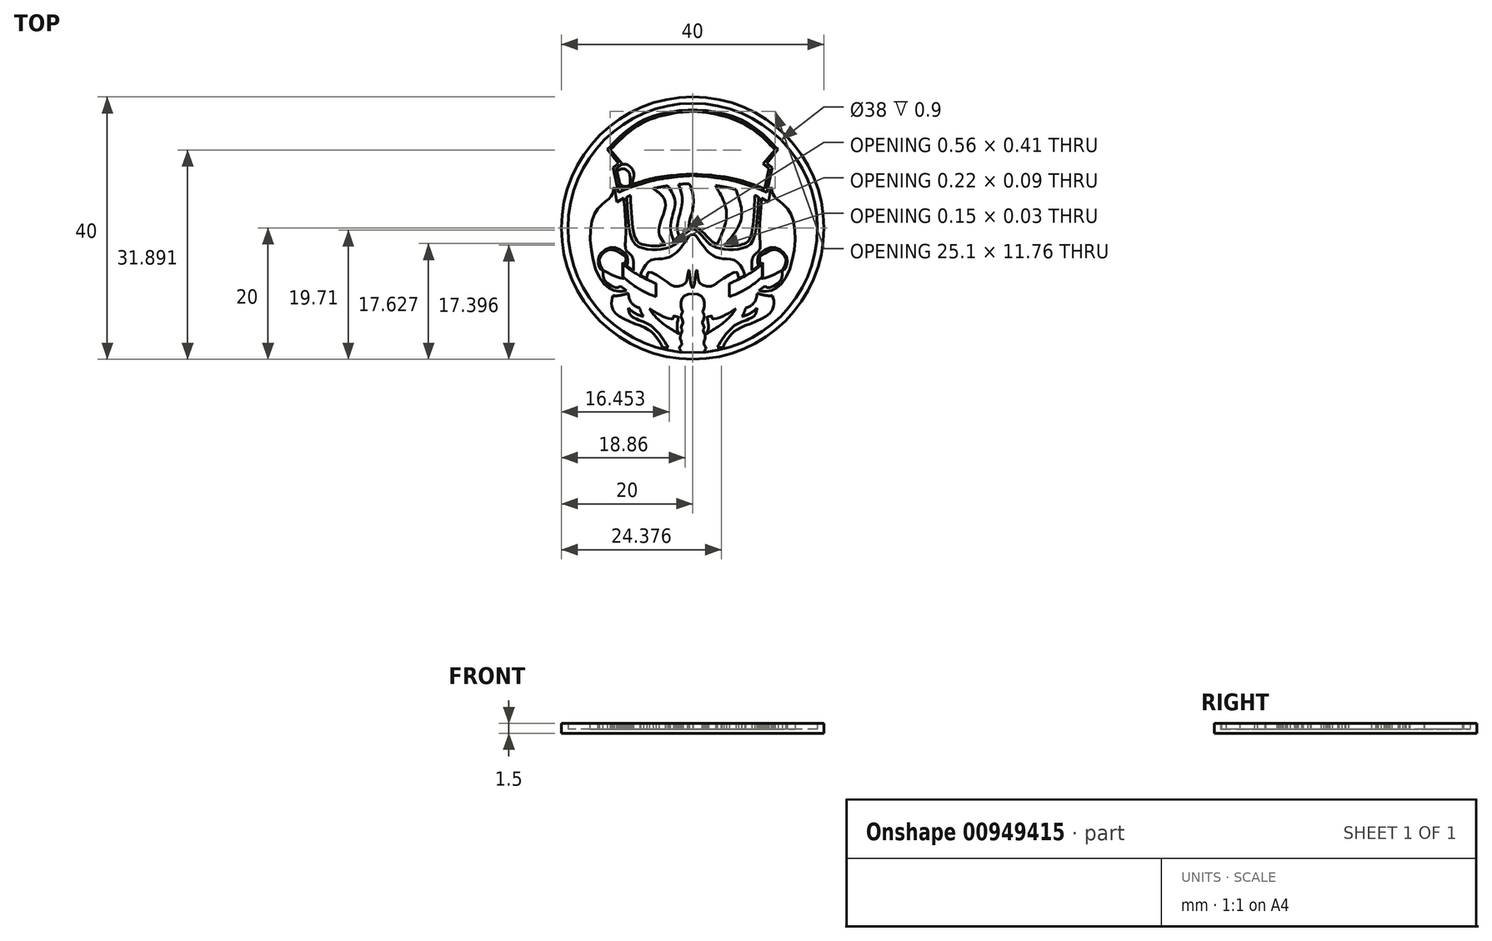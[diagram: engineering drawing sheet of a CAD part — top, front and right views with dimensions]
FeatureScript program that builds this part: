
annotation { "Feature Type Name" : "Feature", "Feature Type Description" : "" }
export const myFeature = defineFeature(function(context is Context, id is Id, definition is map)
    precondition{}
    {
        {
            var Q0;
            Q0=qCreatedBy(makeId("Top.planeOp"),FACE);
            var sketch = newSketch(context, id + "F0", { "sketchPlane" : qUnion([Q0])});
            skCircle(sketch, "E0", {"center": v(0, 0) * mm, "radius": 20 * mm});
            skSolve(sketch);
        }
        {
            var Q0;
            Q0=makeQuery(id+"F0.imprint","IMPRINT",FACE,{"disambiguationData":[TD([[makeQuery(id+"F0.imprint","IMPRINT",EDGE,{"derivedFrom":sQuery(id+"F0.wireOp",EDGE,"E0")}),1.0]])]});
            extrude(context, id + "F1", {"entities" : qUnion([Q0]), "oppositeDirection" : true, "depth" : 0.6 * mm, "offsetDistance" : 25 * mm});
        }
        {
            var Q0;
            Q0=qCreatedBy(makeId("Top.planeOp"),FACE);
            var sketch = newSketch(context, id + "F2", { "sketchPlane" : qUnion([Q0])});
            skCircle(sketch, "E1", {"center": v(0, 0) * mm, "radius": 20 * mm});
            skCircle(sketch, "E2", {"center": v(0, 0) * mm, "radius": 19 * mm});
            skSolve(sketch);
        }
        {
            var Q0;
            Q0=makeQuery(id+"F2.imprint","IMPRINT",FACE,{"disambiguationData":[TD([[makeQuery(id+"F2.imprint","IMPRINT",EDGE,{"derivedFrom":sQuery(id+"F2.wireOp",EDGE,"E1")}),1.0]])]});
            extrude(context, id + "F3", {"entities" : qUnion([Q0]), "operationType" : NewBodyOperationType.ADD, "depth" : 0.9 * mm, "offsetDistance" : 25 * mm});
        }
        {
            var Q0;
            Q0=makeQuery(id+"F2.imprint","IMPRINT",FACE,{"disambiguationData":[TD([[makeQuery(id+"F2.imprint","IMPRINT",EDGE,{"derivedFrom":sQuery(id+"F2.wireOp",EDGE,"E2")}),1.0]])]});
            var sketch = newSketch(context, id + "F4", { "sketchPlane" : qUnion([Q0])});
            skFitSpline(sketch, "E3", {"points": [v(-10, 6) * mm, v(-5.39, 7.38) * mm, v(0, 8) * mm], "startDerivative": vector(9.29, 3.19) * mm, "endDerivative": vector(10.7, 0.84) * mm});
            skFitSpline(sketch, "E4", {"points": [v(0, 18) * mm, v(-8.23, 16.1) * mm, v(-13, 12) * mm], "startDerivative": vector(-15.55, -0.2) * mm, "endDerivative": vector(-7.67, -7.65) * mm});
            skLineSegment(sketch, "E5", {"start": v(-13, 12) * mm, "end": v(-11.31, 9.82) * mm});
            skLineSegment(sketch, "E6", {"start": v(-11.31, 9.82) * mm, "end": v(-12.11, 9.24) * mm});
            skLineSegment(sketch, "E7", {"start": v(-12.11, 9.24) * mm, "end": v(-11.3, 5.42) * mm});
            skFitSpline(sketch, "E8", {"points": [v(-11.3, 5.42) * mm, v(-10.6, 5.73) * mm, v(-10, 6) * mm], "startDerivative": vector(1.26, 0.65) * mm, "endDerivative": vector(1.34, 0.5) * mm});
            skFitSpline(sketch, "E9", {"points": [v(0, -10) * mm, v(-1.55, -10.67) * mm, v(-1.74, -12.16) * mm, v(-1.55, -12.82) * mm, v(-1.8, -13.5) * mm, v(-1.48, -14.4) * mm, v(-1.78, -15.2) * mm, v(-1.56, -15.53) * mm, v(-1.93, -16.52) * mm, v(-1.65, -17.67) * mm, v(-2.04, -18.27) * mm, v(-1.77, -18.78) * mm, v(-1.7, -18.92) * mm], "startDerivative": vector(-18.9, 0.07) * mm, "endDerivative": vector(0.8, -5.27) * mm});
            skFitSpline(sketch, "E10", {"points": [v(-10.6, -5.4) * mm, v(-8.6, -6.97) * mm, v(-5.6, -8.45) * mm], "startDerivative": vector(3.56, -4.4) * mm, "endDerivative": vector(5.98, -2.44) * mm});
            skFitSpline(sketch, "E11", {"points": [v(-5.6, -8.45) * mm, v(-5.6, -10.45) * mm], "startDerivative": vector(0, -2.9) * mm, "endDerivative": vector(0, -2.9) * mm});
            skFitSpline(sketch, "E12", {"points": [v(-5.6, -10.45) * mm, v(-8.7, -8.93) * mm, v(-10.6, -7.4) * mm], "startDerivative": vector(-7.12, 2.4) * mm, "endDerivative": vector(-2.94, 3.33) * mm});
            skFitSpline(sketch, "E13", {"points": [v(-10.6, -7.4) * mm, v(-10.6, -5.4) * mm], "startDerivative": vector(0, 3.7) * mm, "endDerivative": vector(0, 3.7) * mm});
            skFitSpline(sketch, "E14", {"points": [v(-10.2, -5.83) * mm, v(-10.2, -4.51) * mm, v(-10.33, -4.25) * mm, v(-12.32, -3.28) * mm, v(-12.86, -3.34) * mm, v(-13.1, -3.44) * mm, v(-14.2, -4.61) * mm, v(-13.84, -6.22) * mm, v(-13.55, -6.45) * mm, v(-11.2, -7.6) * mm, v(-10.58, -7.7) * mm, v(-10.37, -7.64) * mm], "startDerivative": vector(0.17, 16.35) * mm, "endDerivative": vector(6.44, 3.14) * mm});
            skFitSpline(sketch, "E15", {"points": [v(-10.2, -5.77) * mm, v(-10.67, -5.26) * mm], "startDerivative": vector(-0.46, 0.52) * mm, "endDerivative": vector(-0.46, 0.52) * mm});
            skFitSpline(sketch, "E16", {"points": [v(-10.67, -5.26) * mm, v(-10.67, -7.43) * mm], "startDerivative": vector(0, -2.17) * mm, "endDerivative": vector(0, -2.17) * mm});
            skFitSpline(sketch, "E17", {"points": [v(-10.67, -7.43) * mm, v(-10.49, -7.68) * mm], "startDerivative": vector(0.18, -0.25) * mm, "endDerivative": vector(0.18, -0.25) * mm});
            skFitSpline(sketch, "E18", {"points": [v(0, -1) * mm, v(-0.45, -1.12) * mm, v(-1, -1.92) * mm, v(-1.96, -3.18) * mm, v(-2.84, -4) * mm, v(-4.46, -4.67) * mm, v(-6.52, -5) * mm, v(-7.75, -6.63) * mm, v(-7.94, -7.19) * mm], "startDerivative": vector(-6.21, -0.46) * mm, "endDerivative": vector(-1.36, -5.4) * mm});
            skFitSpline(sketch, "E19", {"points": [v(-7.94, -7.19) * mm, v(-7.5, -7.44) * mm, v(-6.97, -7.68) * mm], "startDerivative": vector(0.9, -0.52) * mm, "endDerivative": vector(1.11, -0.56) * mm});
            skFitSpline(sketch, "E20", {"points": [v(-6.97, -7.68) * mm, v(-6.73, -6.75) * mm, v(-4.37, -7.9) * mm, v(-2.53, -8.9) * mm, v(-1.08, -8.4) * mm, v(-0.82, -7.58) * mm, v(-0.69, -6.9) * mm, v(-0.6, -6.42) * mm, v(-0.46, -6.93) * mm, v(-0.4, -7.6) * mm, v(-0.3, -8.24) * mm, v(0, -9.17) * mm], "startDerivative": vector(1.58, 11.88) * mm, "endDerivative": vector(6.72, -1.02) * mm});
            skFitSpline(sketch, "E21", {"points": [v(-2.1, -16.14) * mm, v(-5.13, -14.06) * mm, v(-6.6, -12.3) * mm], "startDerivative": vector(-6.01, 3.64) * mm, "endDerivative": vector(-2.86, 4.07) * mm});
            skFitSpline(sketch, "E22", {"points": [v(-6.6, -12.3) * mm, v(-4.55, -13.45) * mm, v(-3, -13.8) * mm, v(-2.92, -13.45) * mm, v(-2.89, -13.42) * mm, v(-2.26, -13.53) * mm, v(-2.19, -13.63) * mm, v(-2.4, -15.03) * mm, v(-2.1, -16.14) * mm], "startDerivative": vector(8.79, -5.51) * mm, "endDerivative": vector(2.89, -6.3) * mm});
            skFitSpline(sketch, "E23", {"points": [v(-1.7, -18.92) * mm, v(-0.73, -18.96) * mm, v(0, -19) * mm], "startDerivative": vector(1.88, -0.08) * mm, "endDerivative": vector(1.52, -0.06) * mm});
            skFitSpline(sketch, "E24", {"points": [v(0, -19) * mm, v(0, -10) * mm], "startDerivative": vector(0, 9) * mm, "endDerivative": vector(0, 9) * mm});
            skFitSpline(sketch, "E25", {"points": [v(0, 0) * mm, v(-0.55, -0.43) * mm, v(-1.08, -0.82) * mm, v(-2, -1.88) * mm, v(-3, -2.7) * mm, v(-4.2, -3.11) * mm, v(-5.9, -3.3) * mm, v(-7.85, -3) * mm, v(-9.19, -1.89) * mm, v(-10, 4.76) * mm], "startDerivative": vector(-7.84, -6.38) * mm, "endDerivative": vector(-1.16, 36.52) * mm});
            skFitSpline(sketch, "E26", {"points": [v(-9.49, 4.98) * mm, v(-8.7, -1.64) * mm, v(-7.7, -2.46) * mm, v(-5.91, -2.72) * mm, v(-4.3, -2.59) * mm, v(-3.13, -2.17) * mm, v(-2.38, -1.48) * mm, v(-1.42, -0.5) * mm, v(-0.86, -0.09) * mm, v(0, 0.5) * mm], "startDerivative": vector(1.45, -36.14) * mm, "endDerivative": vector(10.4, 7.12) * mm});
            skFitSpline(sketch, "E27", {"points": [v(0, 0.5) * mm, v(0, 0) * mm], "startDerivative": vector(0, -0.48) * mm, "endDerivative": vector(0, -0.48) * mm});
            skFitSpline(sketch, "E28", {"points": [v(-10, 4.76) * mm, v(-9.69, 4.9) * mm, v(-9.49, 4.98) * mm], "startDerivative": vector(0.6, 0.3) * mm, "endDerivative": vector(0.5, 0.1) * mm});
            skFitSpline(sketch, "E29", {"points": [v(0, 8.27) * mm, v(-5.45, 7.7) * mm, v(-8.57, 6.86) * mm, v(-10.06, 6.34) * mm, v(-10.66, 6.12) * mm, v(-11, 6) * mm], "startDerivative": vector(-16.74, -1.24) * mm, "endDerivative": vector(-3.62, -1.2) * mm});
            skFitSpline(sketch, "E30", {"points": [v(-11, 6) * mm, v(-11.51, 8.55) * mm, v(-11.53, 8.63) * mm, v(-11.53, 8.64) * mm, v(-11.62, 9.09) * mm], "startDerivative": vector(-0.63, 3.1) * mm, "endDerivative": vector(-0.63, 3.1) * mm});
            skFitSpline(sketch, "E31", {"points": [v(-11.62, 9.09) * mm, v(-10.71, 9.77) * mm], "startDerivative": vector(0.91, 0.68) * mm, "endDerivative": vector(0.91, 0.68) * mm});
            skFitSpline(sketch, "E32", {"points": [v(-10.71, 9.77) * mm, v(-12.55, 11.95) * mm], "startDerivative": vector(-1.84, 2.18) * mm, "endDerivative": vector(-1.84, 2.18) * mm});
            skFitSpline(sketch, "E33", {"points": [v(-12.55, 11.95) * mm, v(-8, 15.84) * mm, v(-2.77, 17.51) * mm, v(0, 17.77) * mm], "startDerivative": vector(8.59, 8.8) * mm, "endDerivative": vector(14.03, 0.53) * mm});
            skFitSpline(sketch, "E34", {"points": [v(0, 18) * mm, v(0, 17.77) * mm], "startDerivative": vector(0, -0.2) * mm, "endDerivative": vector(0, -0.2) * mm});
            skFitSpline(sketch, "E35", {"points": [v(0, -1) * mm, v(0, -9.17) * mm], "startDerivative": vector(0, -8.17) * mm, "endDerivative": vector(0, -8.17) * mm});
            skFitSpline(sketch, "E36", {"points": [v(-11.92, 6.25) * mm, v(-11.53, 3.94) * mm], "startDerivative": vector(0.4, -2.32) * mm, "endDerivative": vector(0.4, -2.32) * mm});
            skFitSpline(sketch, "E37", {"points": [v(-11.53, 3.94) * mm, v(-10.48, 4.6) * mm], "startDerivative": vector(0.7, 0.46) * mm, "endDerivative": vector(0.7, 0.46) * mm});
            skFitSpline(sketch, "E38", {"points": [v(-10.48, 4.6) * mm, v(-10.2, -1.29) * mm, v(-9.76, -3.75) * mm], "startDerivative": vector(0.6, -12.73) * mm, "endDerivative": vector(5.35, -2.2) * mm});
            skFitSpline(sketch, "E39", {"points": [v(-9.76, -3.75) * mm, v(-9.25, -4.3) * mm, v(-9, -6.47) * mm], "startDerivative": vector(0.73, -0.96) * mm, "endDerivative": vector(-0.02, -5.18) * mm});
            skFitSpline(sketch, "E40", {"points": [v(-9, -6.47) * mm, v(-10.05, -5.78) * mm], "startDerivative": vector(-1.27, 0.8) * mm, "endDerivative": vector(-1.27, 0.8) * mm});
            skFitSpline(sketch, "E41", {"points": [v(-10.05, -5.78) * mm, v(-9.9, -4.53) * mm, v(-10.15, -4) * mm, v(-12.16, -2.95) * mm, v(-14.34, -4.5) * mm, v(-13.98, -6.28) * mm, v(-13.65, -6.56) * mm, v(-13.54, -7.77) * mm, v(-11.55, -9.1) * mm, v(-11.07, -8.84) * mm], "startDerivative": vector(4.02, 12.53) * mm, "endDerivative": vector(4.81, 5.83) * mm});
            skFitSpline(sketch, "E42", {"points": [v(-11.07, -8.84) * mm, v(-10.1, -9.5) * mm], "startDerivative": vector(0.98, -0.66) * mm, "endDerivative": vector(0.98, -0.66) * mm});
            skFitSpline(sketch, "E43", {"points": [v(-10.1, -9.5) * mm, v(-10.48, -9.64) * mm, v(-13.41, -8.63) * mm, v(-15.14, 1.76) * mm, v(-12.61, 4.6) * mm, v(-12.18, 5.33) * mm, v(-11.92, 6.25) * mm], "startDerivative": vector(-6.35, -3.45) * mm, "endDerivative": vector(3.02, 14.36) * mm});
            skFitSpline(sketch, "E44", {"points": [v(-9.83, -9.93) * mm, v(-9.41, -11.29) * mm, v(-8.08, -12.16) * mm], "startDerivative": vector(0.45, -2.64) * mm, "endDerivative": vector(2.57, -0.47) * mm});
            skFitSpline(sketch, "E45", {"points": [v(-8.08, -12.16) * mm, v(-7.87, -12.82) * mm, v(-7.51, -13.44) * mm], "startDerivative": vector(0.48, -1.51) * mm, "endDerivative": vector(0.87, -1.14) * mm});
            skFitSpline(sketch, "E46", {"points": [v(-7.51, -13.44) * mm, v(-9.04, -12.8) * mm, v(-9.8, -12.17) * mm], "startDerivative": vector(-2.8, 0.16) * mm, "endDerivative": vector(-1.47, 1.58) * mm});
            skFitSpline(sketch, "E47", {"points": [v(-9.8, -12.17) * mm, v(-9.29, -13.46) * mm, v(-6.63, -14.7) * mm, v(-3.71, -18.18) * mm], "startDerivative": vector(0.92, -6.13) * mm, "endDerivative": vector(6.12, -9.7) * mm});
            skFitSpline(sketch, "E48", {"points": [v(-9.83, -9.93) * mm, v(-10.84, -10.23) * mm, v(-12.13, -10.29) * mm], "startDerivative": vector(-1.95, -0.73) * mm, "endDerivative": vector(-2.65, 0.4) * mm});
            skFitSpline(sketch, "E49", {"points": [v(-12.13, -10.29) * mm, v(-12.38, -11.28) * mm, v(-11.64, -13.1) * mm, v(-7.47, -15.1) * mm, v(-5.8, -16.32) * mm, v(-4.74, -17.84) * mm, v(-4.6, -18.18) * mm, v(-3.71, -18.18) * mm], "startDerivative": vector(-2.76, -7.83) * mm, "endDerivative": vector(10.65, 1.36) * mm});
            skLineSegment(sketch, "E50", {"start": v(0, 8.27) * mm, "end": v(0, 8) * mm});
            skFitSpline(sketch, "E51.MirrorCS", {"points": [v(10.67, -7.43) * mm, v(10.49, -7.68) * mm], "startDerivative": vector(-0.18, -0.25) * mm, "endDerivative": vector(-0.18, -0.25) * mm});
            skFitSpline(sketch, "E52.MirrorCS", {"points": [v(10.67, -5.26) * mm, v(10.67, -7.43) * mm], "startDerivative": vector(0, -2.17) * mm, "endDerivative": vector(0, -2.17) * mm});
            skFitSpline(sketch, "E53.MirrorCS", {"points": [v(10.6, -7.4) * mm, v(10.6, -5.4) * mm], "startDerivative": vector(0, 3.7) * mm, "endDerivative": vector(0, 3.7) * mm});
            skFitSpline(sketch, "E54.MirrorCS", {"points": [v(10.2, -5.77) * mm, v(10.67, -5.26) * mm], "startDerivative": vector(0.46, 0.52) * mm, "endDerivative": vector(0.46, 0.52) * mm});
            skFitSpline(sketch, "E55.MirrorCS", {"points": [v(0, 0.5) * mm, v(0, 0) * mm], "startDerivative": vector(0, -0.48) * mm, "endDerivative": vector(0, -0.48) * mm});
            skFitSpline(sketch, "E56.MirrorCS", {"points": [v(11.07, -8.84) * mm, v(10.1, -9.5) * mm], "startDerivative": vector(-0.98, -0.66) * mm, "endDerivative": vector(-0.98, -0.66) * mm});
            skFitSpline(sketch, "E57.MirrorCS", {"points": [v(8.08, -12.16) * mm, v(7.87, -12.82) * mm, v(7.51, -13.44) * mm], "startDerivative": vector(-0.48, -1.51) * mm, "endDerivative": vector(-0.87, -1.14) * mm});
            skFitSpline(sketch, "E58.MirrorCS", {"points": [v(11.3, 5.42) * mm, v(10.6, 5.73) * mm, v(10, 6) * mm], "startDerivative": vector(-1.26, 0.65) * mm, "endDerivative": vector(-1.34, 0.5) * mm});
            skFitSpline(sketch, "E59.MirrorCS", {"points": [v(7.94, -7.19) * mm, v(7.5, -7.44) * mm, v(6.97, -7.68) * mm], "startDerivative": vector(-0.9, -0.52) * mm, "endDerivative": vector(-1.11, -0.56) * mm});
            skFitSpline(sketch, "E60.MirrorCS", {"points": [v(10, 4.76) * mm, v(9.69, 4.9) * mm, v(9.49, 4.98) * mm], "startDerivative": vector(-0.6, 0.3) * mm, "endDerivative": vector(-0.5, 0.1) * mm});
            skFitSpline(sketch, "E61.MirrorCS", {"points": [v(9, -6.47) * mm, v(10.05, -5.78) * mm], "startDerivative": vector(1.27, 0.8) * mm, "endDerivative": vector(1.27, 0.8) * mm});
            skFitSpline(sketch, "E62.MirrorCS", {"points": [v(11.53, 3.94) * mm, v(10.48, 4.6) * mm], "startDerivative": vector(-0.7, 0.46) * mm, "endDerivative": vector(-0.7, 0.46) * mm});
            skFitSpline(sketch, "E63.MirrorCS", {"points": [v(1.7, -18.92) * mm, v(0.73, -18.96) * mm, v(0, -19) * mm], "startDerivative": vector(-1.88, -0.08) * mm, "endDerivative": vector(-1.52, -0.06) * mm});
            skFitSpline(sketch, "E64.MirrorCS", {"points": [v(11.62, 9.09) * mm, v(10.71, 9.77) * mm], "startDerivative": vector(-0.91, 0.68) * mm, "endDerivative": vector(-0.91, 0.68) * mm});
            skFitSpline(sketch, "E65.MirrorCS", {"points": [v(9.83, -9.93) * mm, v(10.84, -10.23) * mm, v(12.13, -10.29) * mm], "startDerivative": vector(1.95, -0.73) * mm, "endDerivative": vector(2.65, 0.4) * mm});
            skFitSpline(sketch, "E66.MirrorCS", {"points": [v(11.92, 6.25) * mm, v(11.53, 3.94) * mm], "startDerivative": vector(-0.4, -2.32) * mm, "endDerivative": vector(-0.4, -2.32) * mm});
            skFitSpline(sketch, "E67.MirrorCS", {"points": [v(7.51, -13.44) * mm, v(9.04, -12.8) * mm, v(9.8, -12.17) * mm], "startDerivative": vector(2.8, 0.16) * mm, "endDerivative": vector(1.47, 1.58) * mm});
            skLineSegment(sketch, "E68.MirrorCS", {"start": v(11.31, 9.82) * mm, "end": v(12.11, 9.24) * mm});
            skFitSpline(sketch, "E69.MirrorCS", {"points": [v(5.6, -8.45) * mm, v(5.6, -10.45) * mm], "startDerivative": vector(0, -2.9) * mm, "endDerivative": vector(0, -2.9) * mm});
            skFitSpline(sketch, "E70.MirrorCS", {"points": [v(10.6, -5.4) * mm, v(8.6, -6.97) * mm, v(5.6, -8.45) * mm], "startDerivative": vector(-3.56, -4.4) * mm, "endDerivative": vector(-5.98, -2.44) * mm});
            skFitSpline(sketch, "E71.MirrorCS", {"points": [v(9.83, -9.93) * mm, v(9.41, -11.29) * mm, v(8.08, -12.16) * mm], "startDerivative": vector(-0.45, -2.64) * mm, "endDerivative": vector(-2.57, -0.47) * mm});
            skFitSpline(sketch, "E72.MirrorCS", {"points": [v(10.71, 9.77) * mm, v(12.55, 11.95) * mm], "startDerivative": vector(1.84, 2.18) * mm, "endDerivative": vector(1.84, 2.18) * mm});
            skLineSegment(sketch, "E73.MirrorCS", {"start": v(13, 12) * mm, "end": v(11.31, 9.82) * mm});
            skLineSegment(sketch, "E74.MirrorCS", {"start": v(12.11, 9.24) * mm, "end": v(11.3, 5.42) * mm});
            skFitSpline(sketch, "E75.MirrorCS", {"points": [v(9.76, -3.75) * mm, v(9.25, -4.3) * mm, v(9, -6.47) * mm], "startDerivative": vector(-0.73, -0.96) * mm, "endDerivative": vector(0.02, -5.18) * mm});
            skFitSpline(sketch, "E76.MirrorCS", {"points": [v(11, 6) * mm, v(11.62, 9.09) * mm], "startDerivative": vector(0.63, 3.1) * mm, "endDerivative": vector(0.63, 3.1) * mm});
            skFitSpline(sketch, "E77.MirrorCS", {"points": [v(2.1, -16.14) * mm, v(5.13, -14.06) * mm, v(6.6, -12.3) * mm], "startDerivative": vector(6.01, 3.64) * mm, "endDerivative": vector(2.86, 4.07) * mm});
            skFitSpline(sketch, "E78.MirrorCS", {"points": [v(12.13, -10.29) * mm, v(12.38, -11.28) * mm, v(11.64, -13.1) * mm, v(7.47, -15.1) * mm, v(5.8, -16.32) * mm, v(4.74, -17.84) * mm, v(4.6, -18.18) * mm, v(3.71, -18.18) * mm], "startDerivative": vector(2.76, -7.83) * mm, "endDerivative": vector(-10.65, 1.36) * mm});
            skFitSpline(sketch, "E79.MirrorCS", {"points": [v(0, -1) * mm, v(0.45, -1.12) * mm, v(1, -1.92) * mm, v(1.96, -3.18) * mm, v(2.84, -4) * mm, v(4.46, -4.67) * mm, v(6.52, -5) * mm, v(7.75, -6.63) * mm, v(7.94, -7.19) * mm], "startDerivative": vector(6.21, -0.46) * mm, "endDerivative": vector(1.36, -5.4) * mm});
            skFitSpline(sketch, "E80.MirrorCS", {"points": [v(10.05, -5.78) * mm, v(9.9, -4.53) * mm, v(10.15, -4) * mm, v(12.16, -2.95) * mm, v(14.34, -4.5) * mm, v(13.98, -6.28) * mm, v(13.65, -6.56) * mm, v(13.54, -7.77) * mm, v(11.55, -9.1) * mm, v(11.07, -8.84) * mm], "startDerivative": vector(-4.02, 12.53) * mm, "endDerivative": vector(-4.81, 5.83) * mm});
            skFitSpline(sketch, "E81.MirrorCS", {"points": [v(0, -19) * mm, v(0, -10) * mm], "startDerivative": vector(0, 9) * mm, "endDerivative": vector(0, 9) * mm});
            skFitSpline(sketch, "E82.MirrorCS", {"points": [v(9.8, -12.17) * mm, v(9.29, -13.46) * mm, v(6.63, -14.7) * mm, v(3.71, -18.18) * mm], "startDerivative": vector(-0.92, -6.13) * mm, "endDerivative": vector(-6.12, -9.7) * mm});
            skFitSpline(sketch, "E83.MirrorCS", {"points": [v(6.6, -12.3) * mm, v(4.55, -13.45) * mm, v(3, -13.8) * mm, v(2.92, -13.45) * mm, v(2.89, -13.42) * mm, v(2.26, -13.53) * mm, v(2.19, -13.63) * mm, v(2.4, -15.03) * mm, v(2.1, -16.14) * mm], "startDerivative": vector(-8.79, -5.51) * mm, "endDerivative": vector(-2.89, -6.3) * mm});
            skFitSpline(sketch, "E84.MirrorCS", {"points": [v(0, -1) * mm, v(0, -9.17) * mm], "startDerivative": vector(0, -8.17) * mm, "endDerivative": vector(0, -8.17) * mm});
            skFitSpline(sketch, "E85.MirrorCS", {"points": [v(0, -10) * mm, v(1.55, -10.67) * mm, v(1.74, -12.16) * mm, v(1.55, -12.82) * mm, v(1.8, -13.5) * mm, v(1.48, -14.4) * mm, v(1.78, -15.2) * mm, v(1.56, -15.53) * mm, v(1.93, -16.52) * mm, v(1.65, -17.67) * mm, v(2.04, -18.27) * mm, v(1.77, -18.78) * mm, v(1.7, -18.92) * mm], "startDerivative": vector(18.9, 0.07) * mm, "endDerivative": vector(-0.8, -5.27) * mm});
            skFitSpline(sketch, "E86.MirrorCS", {"points": [v(5.6, -10.45) * mm, v(8.7, -8.93) * mm, v(10.6, -7.4) * mm], "startDerivative": vector(7.12, 2.4) * mm, "endDerivative": vector(2.94, 3.33) * mm});
            skFitSpline(sketch, "E87.MirrorCS", {"points": [v(10.1, -9.5) * mm, v(10.48, -9.64) * mm, v(13.41, -8.63) * mm, v(15.14, 1.76) * mm, v(12.61, 4.6) * mm, v(12.18, 5.33) * mm, v(11.92, 6.25) * mm], "startDerivative": vector(6.35, -3.45) * mm, "endDerivative": vector(-3.02, 14.36) * mm});
            skFitSpline(sketch, "E88.MirrorCS", {"points": [v(10, 6) * mm, v(5.39, 7.38) * mm, v(0, 8) * mm], "startDerivative": vector(-9.29, 3.19) * mm, "endDerivative": vector(-10.7, 0.84) * mm});
            skFitSpline(sketch, "E89.MirrorCS", {"points": [v(10.48, 4.6) * mm, v(10.2, -1.29) * mm, v(9.76, -3.75) * mm], "startDerivative": vector(-0.6, -12.73) * mm, "endDerivative": vector(-5.35, -2.2) * mm});
            skFitSpline(sketch, "E90.MirrorCS", {"points": [v(6.97, -7.68) * mm, v(6.73, -6.75) * mm, v(4.37, -7.9) * mm, v(2.53, -8.9) * mm, v(1.08, -8.4) * mm, v(0.82, -7.58) * mm, v(0.69, -6.9) * mm, v(0.6, -6.42) * mm, v(0.46, -6.93) * mm, v(0.4, -7.6) * mm, v(0.3, -8.24) * mm, v(0, -9.17) * mm], "startDerivative": vector(-1.58, 11.88) * mm, "endDerivative": vector(-6.72, -1.02) * mm});
            skFitSpline(sketch, "E91.MirrorCS", {"points": [v(0, 8.27) * mm, v(5.45, 7.7) * mm, v(8.57, 6.86) * mm, v(10.06, 6.34) * mm, v(10.66, 6.12) * mm, v(11, 6) * mm], "startDerivative": vector(16.74, -1.24) * mm, "endDerivative": vector(3.62, -1.2) * mm});
            skFitSpline(sketch, "E92.MirrorCS", {"points": [v(0, 0) * mm, v(0.55, -0.43) * mm, v(1.08, -0.82) * mm, v(2, -1.88) * mm, v(3, -2.7) * mm, v(4.2, -3.11) * mm, v(5.9, -3.3) * mm, v(7.85, -3) * mm, v(9.19, -1.89) * mm, v(10, 4.76) * mm], "startDerivative": vector(7.84, -6.38) * mm, "endDerivative": vector(1.16, 36.52) * mm});
            skFitSpline(sketch, "E93.MirrorCS", {"points": [v(9.49, 4.98) * mm, v(8.7, -1.64) * mm, v(7.7, -2.46) * mm, v(5.91, -2.72) * mm, v(4.3, -2.59) * mm, v(3.13, -2.17) * mm, v(2.38, -1.48) * mm, v(1.42, -0.5) * mm, v(0.86, -0.09) * mm, v(0, 0.5) * mm], "startDerivative": vector(-1.45, -36.14) * mm, "endDerivative": vector(-10.4, 7.12) * mm});
            skFitSpline(sketch, "E94.MirrorCS", {"points": [v(10.2, -5.83) * mm, v(10.2, -4.51) * mm, v(10.33, -4.25) * mm, v(12.32, -3.28) * mm, v(12.86, -3.34) * mm, v(13.1, -3.44) * mm, v(14.2, -4.61) * mm, v(13.84, -6.22) * mm, v(13.55, -6.45) * mm, v(11.2, -7.6) * mm, v(10.58, -7.7) * mm, v(10.37, -7.64) * mm], "startDerivative": vector(-0.17, 16.35) * mm, "endDerivative": vector(-6.44, 3.14) * mm});
            skFitSpline(sketch, "E95.MirrorCS", {"points": [v(12.55, 11.95) * mm, v(8.29, 15.6) * mm, v(0, 17.77) * mm], "startDerivative": vector(-8.05, 8.1) * mm, "endDerivative": vector(-16.78, 0.75) * mm});
            skFitSpline(sketch, "E96.MirrorCS", {"points": [v(0, 18) * mm, v(8.23, 16.1) * mm, v(13, 12) * mm], "startDerivative": vector(15.55, -0.2) * mm, "endDerivative": vector(7.67, -7.65) * mm});
            skFitSpline(sketch, "E97", {"points": [v(-11.55, 8.72) * mm, v(-10.63, 9.03) * mm, v(-9.72, 8.46) * mm, v(-9.56, 6.52) * mm], "startDerivative": vector(3.09, 1.67) * mm, "endDerivative": vector(-0.7, -4.47) * mm});
            skFitSpline(sketch, "E98", {"points": [v(-11.55, 8.72) * mm, v(-11.62, 9.09) * mm], "startDerivative": vector(-0.07, 0.37) * mm, "endDerivative": vector(-0.07, 0.37) * mm});
            skFitSpline(sketch, "E99", {"points": [v(-11.62, 9.09) * mm, v(-10.89, 9.64) * mm], "startDerivative": vector(0.74, 0.55) * mm, "endDerivative": vector(0.74, 0.55) * mm});
            skFitSpline(sketch, "E100", {"points": [v(-10.86, 9.66) * mm, v(-10.25, 9.74) * mm, v(-9.15, 8.9) * mm, v(-9.32, 6.6) * mm], "startDerivative": vector(2.33, 0.63) * mm, "endDerivative": vector(-2.6, -6.9) * mm});
            skFitSpline(sketch, "E101", {"points": [v(-9.32, 6.6) * mm, v(-9.56, 6.52) * mm], "startDerivative": vector(-0.16, -0.05) * mm, "endDerivative": vector(-0.16, -0.05) * mm});
            skFitSpline(sketch, "E102", {"points": [v(-10.06, 6.34) * mm, v(-10.76, 6.45) * mm, v(-11.2, 7.07) * mm], "startDerivative": vector(-1.55, -0.02) * mm, "endDerivative": vector(-0.75, 1.46) * mm});
            skFitSpline(sketch, "E103", {"points": [v(-11.2, 7.07) * mm, v(-11, 6) * mm], "startDerivative": vector(0.22, -1.06) * mm, "endDerivative": vector(0.22, -1.06) * mm});
            skFitSpline(sketch, "E104", {"points": [v(-11, 6) * mm, v(-10.06, 6.34) * mm], "startDerivative": vector(0.93, 0.33) * mm, "endDerivative": vector(0.93, 0.33) * mm});
            skFitSpline(sketch, "E105", {"points": [v(-6.67, 7.8) * mm, v(-9.26, 13.22) * mm, v(-9.28, 13.56) * mm, v(-9.03, 13.9) * mm, v(-7.11, 15.52) * mm, v(0.28, 17.4) * mm, v(4.28, 16.2) * mm, v(4.56, 15.76) * mm, v(2.78, 9.16) * mm, v(1.96, 8.73) * mm, v(-1.93, 8.76) * mm, v(-6.32, 7.8) * mm, v(-6.67, 7.8) * mm]});
            skFitSpline(sketch, "E106", {"points": [v(-0.53, 6.76) * mm, v(0, 2.82) * mm, v(-0.56, 0.12) * mm], "startDerivative": vector(3.47, -5.63) * mm, "endDerivative": vector(0.15, -7.05) * mm});
            skFitSpline(sketch, "E107", {"points": [v(-2.15, 6.66) * mm, v(-1.6, 3.9) * mm, v(-2.37, 0.22) * mm, v(-2.08, -1.15) * mm], "startDerivative": vector(2.68, -7.28) * mm, "endDerivative": vector(2.09, -4.76) * mm});
            skFitSpline(sketch, "E108", {"points": [v(-2.08, -1.15) * mm, v(-1.42, -0.5) * mm, v(-0.86, -0.09) * mm, v(-0.56, 0.12) * mm], "startDerivative": vector(1.6, 1.74) * mm, "endDerivative": vector(1.11, 0.75) * mm});
            skFitSpline(sketch, "E109", {"points": [v(-2.15, 6.66) * mm, v(-1.34, 6.72) * mm, v(-0.53, 6.76) * mm], "startDerivative": vector(1.62, 0.1) * mm, "endDerivative": vector(1.61, 0.11) * mm});
            skFitSpline(sketch, "E110", {"points": [v(-3.79, 6.45) * mm, v(-2.69, 3.8) * mm, v(-3.37, 0.58) * mm, v(-2.9, -2) * mm], "startDerivative": vector(4.9, -7.68) * mm, "endDerivative": vector(2.6, -7.83) * mm});
            skFitSpline(sketch, "E111", {"points": [v(-6, 6.01) * mm, v(-4.15, 3.77) * mm, v(-5.16, -0.32) * mm, v(-4.13, -2.55) * mm], "startDerivative": vector(8.31, -5.88) * mm, "endDerivative": vector(5.49, -6.64) * mm});
            skFitSpline(sketch, "E112", {"points": [v(-4.13, -2.55) * mm, v(-3.44, -2.33) * mm, v(-2.9, -2) * mm], "startDerivative": vector(1.38, 0.37) * mm, "endDerivative": vector(1.06, 0.72) * mm});
            skFitSpline(sketch, "E113", {"points": [v(-6, 6.01) * mm, v(-4.92, 6.25) * mm, v(-3.79, 6.45) * mm], "startDerivative": vector(2.19, 0.46) * mm, "endDerivative": vector(2.26, 0.41) * mm});
            skFitSpline(sketch, "E114", {"points": [v(3.47, 6.5) * mm, v(5.17, 2.17) * mm, v(3.73, -2.44) * mm], "startDerivative": vector(4.97, -8.63) * mm, "endDerivative": vector(-4.43, -9.23) * mm});
            skFitSpline(sketch, "E115", {"points": [v(6.6, 5.87) * mm, v(7.4, 1.47) * mm, v(4.84, -2.68) * mm], "startDerivative": vector(3.26, -9.2) * mm, "endDerivative": vector(-6.7, -7.9) * mm});
            skFitSpline(sketch, "E116", {"points": [v(3.73, -2.44) * mm, v(4.3, -2.59) * mm, v(4.84, -2.68) * mm], "startDerivative": vector(1.13, -0.32) * mm, "endDerivative": vector(1.09, -0.15) * mm});
            skFitSpline(sketch, "E117", {"points": [v(3.47, 6.5) * mm, v(5.12, 6.2) * mm, v(6.6, 5.87) * mm], "startDerivative": vector(3.25, -0.55) * mm, "endDerivative": vector(3, -0.7) * mm});
            skSolve(sketch);
        }
        {
            var Q0;
            Q0 = qSketchRegion(id + "F4", true);
            extrude(context, id + "F5", {"entities" : qUnion([Q0]), "depth" : 0.9 * mm, "offsetDistance" : 25 * mm});
        }
        {
            var Q0;
            Q0=sQuery(id+"F4.wireOp",EDGE,"E105");
            extrude(context, id + "F6", {"bodyType" : ToolBodyType.SURFACE, "surfaceEntities" : qUnion([Q0]), "depth" : 0.9 * mm, "offsetDistance" : 25 * mm});
        }
        {
            var Q0;
            Q0=makeQuery(id+"F4.imprint","IMPRINT",FACE,{"disambiguationData":[TD([[makeQuery(id+"F4.imprint","IMPRINT",EDGE,{"derivedFrom":sQuery(id+"F4.wireOp",EDGE,"E97")}),1.0]])]});
            var Q1;
            Q1=makeQuery(id+"F4.imprint","IMPRINT",FACE,{"disambiguationData":[TD([[makeQuery(id+"F4.imprint","IMPRINT",EDGE,{"derivedFrom":sQuery(id+"F4.wireOp",EDGE,"E102")}),1.0]])]});
            extrude(context, id + "F7", {"entities" : qUnion([Q0, Q1]), "depth" : 0.9 * mm, "offsetDistance" : 25 * mm});
        }
    });
